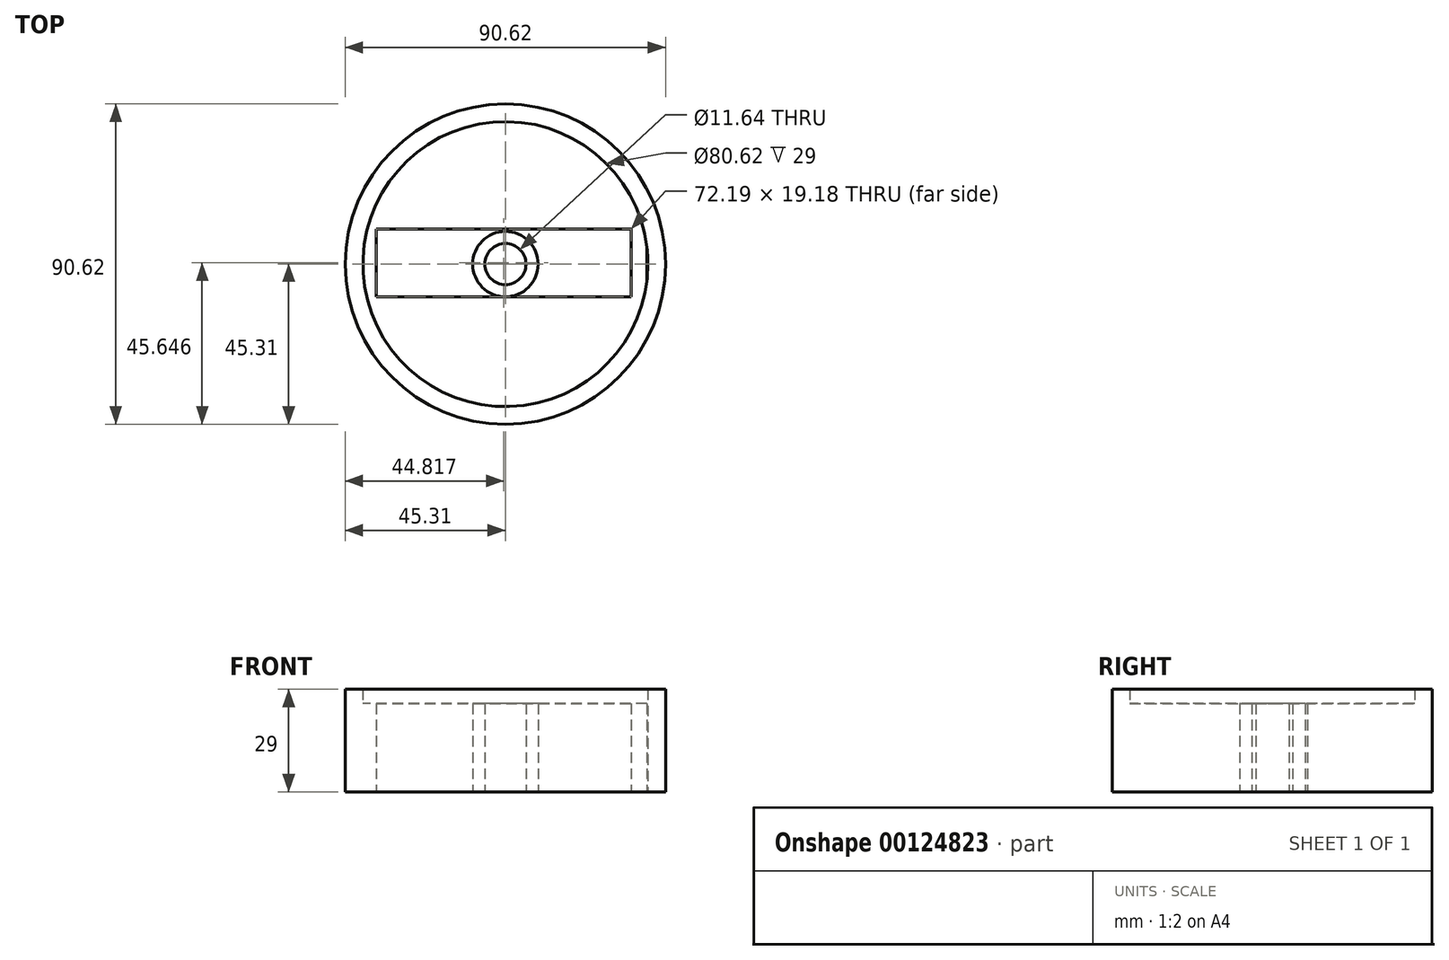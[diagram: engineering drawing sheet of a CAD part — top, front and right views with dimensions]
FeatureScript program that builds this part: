
annotation { "Feature Type Name" : "Feature", "Feature Type Description" : "" }
export const myFeature = defineFeature(function(context is Context, id is Id, definition is map)
    precondition{}
    {
        {
            var Q0;
            Q0=qCreatedBy(makeId("Top.planeOp"),FACE);
            var sketch = newSketch(context, id + "F0", { "sketchPlane" : qUnion([Q0])});
            skCircle(sketch, "E0", {"center": v(0, 4.69) * mm, "radius": 45.31 * mm});
            skCircle(sketch, "E1", {"center": v(0, 4.69) * mm, "radius": 40.31 * mm});
            skLineSegment(sketch, "E2.right", {"start": v(40.04, 10.5) * mm, "end": v(40.04, 0) * mm});
            skLineSegment(sketch, "E3.right", {"start": v(-39.88, 0) * mm, "end": v(-39.88, 10.57) * mm});
            skLineSegment(sketch, "E4.right", {"start": v(141.5, -6.74) * mm, "end": v(141.5, -18.04) * mm});
            skCircle(sketch, "E5", {"center": v(0, 4.69) * mm, "radius": 9.25 * mm});
            skLineSegment(sketch, "E6", {"start": v(0, -4.56) * mm, "end": v(-36.59, -4.56) * mm});
            skLineSegment(sketch, "E7", {"start": v(-36.59, -4.56) * mm, "end": v(35.6, -4.56) * mm});
            skLineSegment(sketch, "E8", {"start": v(-36.59, -4.56) * mm, "end": v(-36.59, 14.62) * mm});
            skLineSegment(sketch, "E9", {"start": v(-36.59, 14.62) * mm, "end": v(35.6, 14.62) * mm});
            skLineSegment(sketch, "E10", {"start": v(35.6, 14.62) * mm, "end": v(35.6, -4.56) * mm});
            skCircle(sketch, "E11", {"center": v(0, 4.69) * mm, "radius": 5.82 * mm});
            skSolve(sketch);
        }
        {
            var Q0;
            Q0 = qSketchRegion(id + "F0", true);
            extrude(context, id + "F1", {"entities" : qUnion([Q0]), "depth" : 29 * mm});
        }
        {
            var Q0;
            Q0 = qSketchRegion(id + "F0", true);
            extrude(context, id + "F2", {"entities" : qUnion([Q0]), "operationType" : NewBodyOperationType.REMOVE, "oppositeDirection" : true, "depth" : 30 * mm});
        }
        {
            var Q0;
            Q0=makeQuery(id+"F0.imprint","IMPRINT",FACE,{"disambiguationData":[TD([[makeQuery(id+"F0.imprint","IMPRINT",EDGE,{"derivedFrom":sQuery(id+"F0.wireOp",EDGE,"E5")}),1.0]])]});
            var Q1;
            {var subQ0=sQuery(id+"F0.wireOp",EDGE,"E8");Q1=makeQuery(id+"F0.imprint","IMPRINT",FACE,{"disambiguationData":[TD([[makeQuery(id+"F0.imprint","IMPRINT",EDGE,{"derivedFrom":subQ0}),1.0]])]});}
            extrude(context, id + "F3", {"entities" : qUnion([Q0, Q1]), "operationType" : NewBodyOperationType.ADD, "depth" : 25 * mm});
        }
    });
